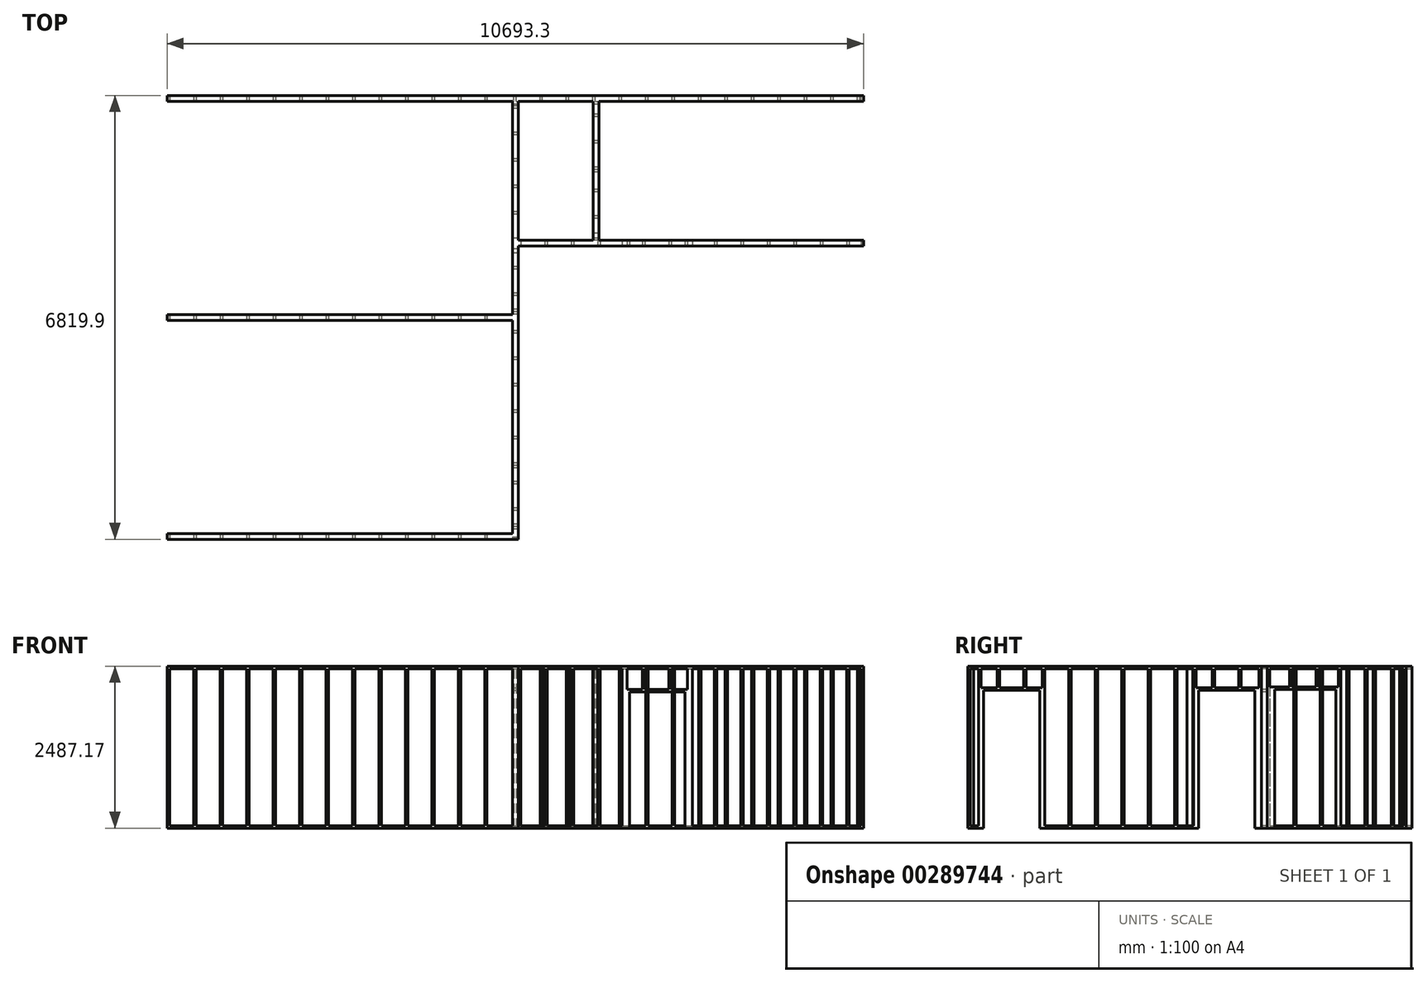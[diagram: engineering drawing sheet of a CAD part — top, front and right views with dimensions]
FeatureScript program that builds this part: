
annotation { "Feature Type Name" : "Feature", "Feature Type Description" : "" }
export const myFeature = defineFeature(function(context is Context, id is Id, definition is map)
    precondition{}
    {
        {
            var Q0;
            Q0=qCreatedBy(makeId("Top.planeOp"),FACE);
            var sketch = newSketch(context, id + "F0", { "sketchPlane" : qUnion([Q0])});
            skLineSegment(sketch, "E0.bottom", {"start": v(5346.65, -4111.3) * mm, "end": v(-5346.65, -4111.3) * mm});
            skLineSegment(sketch, "E0.top", {"start": v(5346.65, 4111.3) * mm, "end": v(-5346.65, 4111.3) * mm});
            skLineSegment(sketch, "E0.left", {"start": v(5346.65, -4111.3) * mm, "end": v(5346.65, 4111.3) * mm});
            skLineSegment(sketch, "E0.right", {"start": v(-5346.65, -4111.3) * mm, "end": v(-5346.65, 4111.3) * mm});
            skPoint(sketch, "E0.middle", {"position": v(0, 0) * mm});
            skLineSegment(sketch, "E1.bottom", {"start": v(-5346.65, 4111.3) * mm, "end": v(5346.65, 4111.3) * mm});
            skLineSegment(sketch, "E1.top", {"start": v(-5346.65, 4022.4) * mm, "end": v(5346.65, 4022.4) * mm});
            skLineSegment(sketch, "E1.left", {"start": v(-5346.65, 4111.3) * mm, "end": v(-5346.65, 4022.4) * mm});
            skLineSegment(sketch, "E1.right", {"start": v(5346.65, 4111.3) * mm, "end": v(5346.65, 4022.4) * mm});
            skLineSegment(sketch, "E2", {"start": v(0, 4111.3) * mm, "end": v(0, -4111.3) * mm, "construction": true});
            skLineSegment(sketch, "E3", {"start": v(-44.45, -2619.7) * mm, "end": v(-5346.65, -2619.7) * mm});
            skLineSegment(sketch, "E4", {"start": v(44.45, 4022.4) * mm, "end": v(44.45, -2708.6) * mm});
            skLineSegment(sketch, "E5", {"start": v(44.45, -2708.6) * mm, "end": v(-5346.65, -2708.6) * mm});
            skLineSegment(sketch, "E6", {"start": v(-44.45, 4022.4) * mm, "end": v(-44.45, -2619.7) * mm});
            skLineSegment(sketch, "E7.bottom", {"start": v(-44.45, 745.8) * mm, "end": v(-5346.65, 745.8) * mm});
            skLineSegment(sketch, "E7.top", {"start": v(-44.45, 656.9) * mm, "end": v(-5346.65, 656.9) * mm});
            skLineSegment(sketch, "E7.left", {"start": v(-44.45, 745.8) * mm, "end": v(-44.45, 656.9) * mm});
            skLineSegment(sketch, "E7.right", {"start": v(-5346.65, 745.8) * mm, "end": v(-5346.65, 656.9) * mm});
            skLineSegment(sketch, "E8.bottom", {"start": v(44.45, 1888.8) * mm, "end": v(5346.65, 1888.8) * mm});
            skLineSegment(sketch, "E8.top", {"start": v(44.45, 1799.9) * mm, "end": v(5346.65, 1799.9) * mm});
            skLineSegment(sketch, "E8.left", {"start": v(44.45, 1888.8) * mm, "end": v(44.45, 1799.9) * mm});
            skLineSegment(sketch, "E8.right", {"start": v(5346.65, 1888.8) * mm, "end": v(5346.65, 1799.9) * mm});
            skLineSegment(sketch, "E9.bottom", {"start": v(1282.55, 1888.8) * mm, "end": v(1193.65, 1888.8) * mm});
            skLineSegment(sketch, "E9.top", {"start": v(1282.55, 4022.4) * mm, "end": v(1193.65, 4022.4) * mm});
            skLineSegment(sketch, "E9.left", {"start": v(1282.55, 1888.8) * mm, "end": v(1282.55, 4022.4) * mm});
            skLineSegment(sketch, "E9.right", {"start": v(1193.65, 1888.8) * mm, "end": v(1193.65, 4022.4) * mm});
            skLineSegment(sketch, "E10", {"start": v(1282.55, 2041.2) * mm, "end": v(1193.65, 2041.2) * mm});
            skLineSegment(sketch, "E11", {"start": v(1282.55, 2955.6) * mm, "end": v(1193.65, 2955.6) * mm});
            skSolve(sketch);
        }
        {
            var Q0;
            {var subQ4=sQuery(id+"F0.wireOp",EDGE,"E0.top");Q0=makeQuery(id+"F0.imprint","IMPRINT",FACE,{"disambiguationData":[TD([[makeQuery(id+"F0.imprint","IMPRINT",EDGE,{"derivedFrom":subQ4}),1.0]])]});}
            var Q1;
            {var subQ7=sQuery(id+"F0.wireOp",EDGE,"E3");Q1=makeQuery(id+"F0.imprint","IMPRINT",FACE,{"disambiguationData":[TD([[makeQuery(id+"F0.imprint","IMPRINT",EDGE,{"derivedFrom":subQ7}),1.0]])]});}
            var Q2;
            {var subQ0=sQuery(id+"F0.wireOp",EDGE,"E8.bottom");Q2=makeQuery(id+"F0.imprint","IMPRINT",FACE,{"disambiguationData":[TD([[makeQuery(id+"F0.imprint","IMPRINT",EDGE,{"derivedFrom":subQ0}),-1.0]])]});}
            var Q3;
            {var subQ0=sQuery(id+"F0.wireOp",EDGE,"E7.bottom");Q3=makeQuery(id+"F0.imprint","IMPRINT",FACE,{"disambiguationData":[TD([[makeQuery(id+"F0.imprint","IMPRINT",EDGE,{"derivedFrom":subQ0}),1.0]])]});}
            var Q4;
            {var subQ5=sQuery(id+"F0.wireOp",EDGE,"E11");Q4=makeQuery(id+"F0.imprint","IMPRINT",FACE,{"disambiguationData":[TD([[makeQuery(id+"F0.imprint","IMPRINT",EDGE,{"derivedFrom":subQ5}),-1.0]])]});}
            var Q5;
            {var subQ5=sQuery(id+"F0.wireOp",EDGE,"E10");Q5=makeQuery(id+"F0.imprint","IMPRINT",FACE,{"disambiguationData":[TD([[makeQuery(id+"F0.imprint","IMPRINT",EDGE,{"derivedFrom":subQ5}),1.0]])]});}
            var Q6;
            {var subQ2=sQuery(id+"F0.wireOp",EDGE,"E10");Q6=makeQuery(id+"F0.imprint","IMPRINT",FACE,{"disambiguationData":[TD([[makeQuery(id+"F0.imprint","IMPRINT",EDGE,{"derivedFrom":subQ2}),-1.0]])]});}
            extrude(context, id + "F1", {"entities" : qUnion([Q0, Q1, Q2, Q3, Q4, Q5, Q6]), "depth" : 2487.17 * mm, "offsetDistance" : 30.48 * mm});
        }
        {
            var Q0;
            {var subQ0=sQuery(id+"F0.wireOp",EDGE,"E4");Q0=makeQuery(id+"F1.opExtrude","SWEPT_FACE",FACE,{"disambiguationData":[OSD([subQ0]),TDD([makeQuery(id+"F0.imprint","IMPRINT",EDGE,{"disambiguationData":[TD([[makeQuery(id+"F0.imprint","INTERSECT",VERTEX,{"derivedFrom":[subQ0,sQuery(id+"F0.wireOp",EDGE,"E8.top")]}),-1.0]])],"derivedFrom":subQ0})])]});}
            var sketch = newSketch(context, id + "F2", { "sketchPlane" : qUnion([Q0])});
            skLineSegment(sketch, "E12.bottom", {"start": v(1698.24, 0) * mm, "end": v(834.75, 0) * mm});
            skLineSegment(sketch, "E12.top", {"start": v(1698.24, 2120.9) * mm, "end": v(834.75, 2120.9) * mm});
            skLineSegment(sketch, "E12.left", {"start": v(1698.24, 0) * mm, "end": v(1698.24, 2120.9) * mm});
            skLineSegment(sketch, "E12.right", {"start": v(834.75, 0) * mm, "end": v(834.75, 2120.9) * mm});
            skLineSegment(sketch, "E13.bottom", {"start": v(-2670.5, 2449.07) * mm, "end": v(758.55, 2449.07) * mm});
            skLineSegment(sketch, "E13.top", {"start": v(-2670.5, 38.1) * mm, "end": v(758.55, 38.1) * mm});
            skLineSegment(sketch, "E13.left", {"start": v(-2670.5, 2449.07) * mm, "end": v(-2670.5, 38.1) * mm});
            skLineSegment(sketch, "E13.right", {"start": v(758.55, 2449.07) * mm, "end": v(758.55, 38.1) * mm});
            skLineSegment(sketch, "E14.bottom", {"start": v(796.65, 2449.07) * mm, "end": v(1761.8, 2449.07) * mm});
            skLineSegment(sketch, "E14.top", {"start": v(796.65, 2159) * mm, "end": v(1761.8, 2159) * mm});
            skLineSegment(sketch, "E14.left", {"start": v(796.65, 2449.07) * mm, "end": v(796.65, 2159) * mm});
            skLineSegment(sketch, "E14.right", {"start": v(1761.8, 2449.07) * mm, "end": v(1761.8, 2159) * mm});
            skLineSegment(sketch, "E15.bottom", {"start": v(-2467.3, 0) * mm, "end": v(-1603.7, 0) * mm});
            skLineSegment(sketch, "E15.top", {"start": v(-2467.3, 2120.9) * mm, "end": v(-1603.7, 2120.9) * mm});
            skLineSegment(sketch, "E15.left", {"start": v(-2467.3, 0) * mm, "end": v(-2467.3, 2120.9) * mm});
            skLineSegment(sketch, "E15.right", {"start": v(-1603.7, 0) * mm, "end": v(-1603.7, 2120.9) * mm});
            skLineSegment(sketch, "E16.bottom", {"start": v(-2467.3, 2120.9) * mm, "end": v(-2505.4, 2120.9) * mm});
            skLineSegment(sketch, "E16.top", {"start": v(-2467.3, 38.1) * mm, "end": v(-2505.4, 38.1) * mm});
            skLineSegment(sketch, "E16.left", {"start": v(-2467.3, 2120.9) * mm, "end": v(-2467.3, 38.1) * mm});
            skLineSegment(sketch, "E16.right", {"start": v(-2505.4, 2120.9) * mm, "end": v(-2505.4, 38.1) * mm});
            skLineSegment(sketch, "E17.bottom", {"start": v(-1603.7, 2120.9) * mm, "end": v(-1565.6, 2120.9) * mm});
            skLineSegment(sketch, "E17.top", {"start": v(-1603.7, 38.1) * mm, "end": v(-1565.6, 38.1) * mm});
            skLineSegment(sketch, "E17.left", {"start": v(-1603.7, 2120.9) * mm, "end": v(-1603.7, 38.1) * mm});
            skLineSegment(sketch, "E17.right", {"start": v(-1565.6, 2120.9) * mm, "end": v(-1565.6, 38.1) * mm});
            skLineSegment(sketch, "E18.bottom", {"start": v(-2505.4, 2120.9) * mm, "end": v(-1565.6, 2120.9) * mm});
            skLineSegment(sketch, "E18.top", {"start": v(-2505.4, 2159) * mm, "end": v(-1565.6, 2159) * mm});
            skLineSegment(sketch, "E18.left", {"start": v(-2505.4, 2120.9) * mm, "end": v(-2505.4, 2159) * mm});
            skLineSegment(sketch, "E18.right", {"start": v(-1565.6, 2120.9) * mm, "end": v(-1565.6, 2159) * mm});
            skLineSegment(sketch, "E19.bottom", {"start": v(-2505.4, 38.1) * mm, "end": v(-2543.5, 38.1) * mm});
            skLineSegment(sketch, "E19.top", {"start": v(-2505.4, 2449.07) * mm, "end": v(-2543.5, 2449.07) * mm});
            skLineSegment(sketch, "E19.left", {"start": v(-2505.4, 38.1) * mm, "end": v(-2505.4, 2449.07) * mm});
            skLineSegment(sketch, "E19.right", {"start": v(-2543.5, 38.1) * mm, "end": v(-2543.5, 2449.07) * mm});
            skLineSegment(sketch, "E20.bottom", {"start": v(-1565.6, 38.1) * mm, "end": v(-1527.5, 38.1) * mm});
            skLineSegment(sketch, "E20.top", {"start": v(-1565.6, 2449.07) * mm, "end": v(-1527.5, 2449.07) * mm});
            skLineSegment(sketch, "E20.left", {"start": v(-1565.6, 38.1) * mm, "end": v(-1565.6, 2449.07) * mm});
            skLineSegment(sketch, "E20.right", {"start": v(-1527.5, 38.1) * mm, "end": v(-1527.5, 2449.07) * mm});
            skLineSegment(sketch, "E21.bottom", {"start": v(-1159.2, 38.1) * mm, "end": v(-1121.1, 38.1) * mm});
            skLineSegment(sketch, "E21.top", {"start": v(-1159.2, 2449.07) * mm, "end": v(-1121.1, 2449.07) * mm});
            skLineSegment(sketch, "E21.left", {"start": v(-1159.2, 38.1) * mm, "end": v(-1159.2, 2449.07) * mm});
            skLineSegment(sketch, "E21.right", {"start": v(-1121.1, 38.1) * mm, "end": v(-1121.1, 2449.07) * mm});
            skLineSegment(sketch, "E22.bottom", {"start": v(-752.9, 38.1) * mm, "end": v(-714.8, 38.1) * mm});
            skLineSegment(sketch, "E22.top", {"start": v(-752.9, 2449.07) * mm, "end": v(-714.8, 2449.07) * mm});
            skLineSegment(sketch, "E22.left", {"start": v(-752.9, 38.1) * mm, "end": v(-752.9, 2449.07) * mm});
            skLineSegment(sketch, "E22.right", {"start": v(-714.8, 38.1) * mm, "end": v(-714.8, 2449.07) * mm});
            skLineSegment(sketch, "E23.bottom", {"start": v(-346.6, 38.1) * mm, "end": v(-308.5, 38.1) * mm});
            skLineSegment(sketch, "E23.top", {"start": v(-346.6, 2449.07) * mm, "end": v(-308.5, 2449.07) * mm});
            skLineSegment(sketch, "E23.left", {"start": v(-346.6, 38.1) * mm, "end": v(-346.6, 2449.07) * mm});
            skLineSegment(sketch, "E23.right", {"start": v(-308.5, 38.1) * mm, "end": v(-308.5, 2449.07) * mm});
            skLineSegment(sketch, "E24.bottom", {"start": v(59.7, 38.1) * mm, "end": v(97.8, 38.1) * mm});
            skLineSegment(sketch, "E24.top", {"start": v(59.7, 2449.07) * mm, "end": v(97.8, 2449.07) * mm});
            skLineSegment(sketch, "E24.left", {"start": v(59.7, 38.1) * mm, "end": v(59.7, 2449.07) * mm});
            skLineSegment(sketch, "E24.right", {"start": v(97.8, 38.1) * mm, "end": v(97.8, 2449.07) * mm});
            skLineSegment(sketch, "E25.bottom", {"start": v(465.99, 2449.07) * mm, "end": v(504.09, 2449.07) * mm});
            skLineSegment(sketch, "E25.top", {"start": v(465.99, 38.1) * mm, "end": v(504.09, 38.1) * mm});
            skLineSegment(sketch, "E25.left", {"start": v(465.99, 2449.07) * mm, "end": v(465.99, 38.1) * mm});
            skLineSegment(sketch, "E25.right", {"start": v(504.09, 2449.07) * mm, "end": v(504.09, 38.1) * mm});
            skLineSegment(sketch, "E26.bottom", {"start": v(-2257.65, 2159) * mm, "end": v(-2219.55, 2159) * mm});
            skLineSegment(sketch, "E26.top", {"start": v(-2257.65, 2449.07) * mm, "end": v(-2219.55, 2449.07) * mm});
            skLineSegment(sketch, "E26.left", {"start": v(-2257.65, 2159) * mm, "end": v(-2257.65, 2449.07) * mm});
            skLineSegment(sketch, "E26.right", {"start": v(-2219.55, 2159) * mm, "end": v(-2219.55, 2449.07) * mm});
            skLineSegment(sketch, "E27.bottom", {"start": v(-1851.36, 2159) * mm, "end": v(-1813.26, 2159) * mm});
            skLineSegment(sketch, "E27.top", {"start": v(-1851.36, 2449.07) * mm, "end": v(-1813.26, 2449.07) * mm});
            skLineSegment(sketch, "E27.left", {"start": v(-1851.36, 2159) * mm, "end": v(-1851.36, 2449.07) * mm});
            skLineSegment(sketch, "E27.right", {"start": v(-1813.26, 2159) * mm, "end": v(-1813.26, 2449.07) * mm});
            skLineSegment(sketch, "E28.bottom", {"start": v(1044.45, 2449.07) * mm, "end": v(1082.55, 2449.07) * mm});
            skLineSegment(sketch, "E28.top", {"start": v(1044.45, 2159) * mm, "end": v(1082.55, 2159) * mm});
            skLineSegment(sketch, "E28.left", {"start": v(1044.45, 2449.07) * mm, "end": v(1044.45, 2159) * mm});
            skLineSegment(sketch, "E28.right", {"start": v(1082.55, 2449.07) * mm, "end": v(1082.55, 2159) * mm});
            skLineSegment(sketch, "E29.bottom", {"start": v(1450.75, 2159) * mm, "end": v(1488.85, 2159) * mm});
            skLineSegment(sketch, "E29.top", {"start": v(1450.75, 2449.07) * mm, "end": v(1488.85, 2449.07) * mm});
            skLineSegment(sketch, "E29.left", {"start": v(1450.75, 2159) * mm, "end": v(1450.75, 2449.07) * mm});
            skLineSegment(sketch, "E29.right", {"start": v(1488.85, 2159) * mm, "end": v(1488.85, 2449.07) * mm});
            skSolve(sketch);
        }
        {
            var Q0;
            Q0=makeQuery(id+"F2.imprint","IMPRINT",FACE,{"disambiguationData":[TD([[makeQuery(id+"F2.imprint","IMPRINT",EDGE,{"derivedFrom":sQuery(id+"F2.wireOp",EDGE,"E12.bottom")}),-1.0]])]});
            var Q1;
            {var subQ5=sQuery(id+"F2.wireOp",EDGE,"E15.top");Q1=makeQuery(id+"F2.imprint","IMPRINT",FACE,{"disambiguationData":[TD([[makeQuery(id+"F2.imprint","IMPRINT",EDGE,{"derivedFrom":subQ5}),-1.0]])]});}
            var Q2;
            {var subQ0=sQuery(id+"F2.wireOp",EDGE,"E19.left");Q2=makeQuery(id+"F2.imprint","IMPRINT",FACE,{"disambiguationData":[TD([[makeQuery(id+"F2.imprint","IMPRINT",EDGE,{"derivedFrom":subQ0}),-1.0]])]});}
            var Q3;
            {var subQ0=sQuery(id+"F2.wireOp",EDGE,"E26.right");Q3=makeQuery(id+"F2.imprint","IMPRINT",FACE,{"disambiguationData":[TD([[makeQuery(id+"F2.imprint","IMPRINT",EDGE,{"derivedFrom":subQ0}),-1.0]])]});}
            var Q4;
            {var subQ0=sQuery(id+"F2.wireOp",EDGE,"E20.left");Q4=makeQuery(id+"F2.imprint","IMPRINT",FACE,{"disambiguationData":[TD([[makeQuery(id+"F2.imprint","IMPRINT",EDGE,{"derivedFrom":subQ0}),1.0]])]});}
            var Q5;
            {var subQ0=sQuery(id+"F2.wireOp",EDGE,"E20.right");Q5=makeQuery(id+"F2.imprint","IMPRINT",FACE,{"disambiguationData":[TD([[makeQuery(id+"F2.imprint","IMPRINT",EDGE,{"derivedFrom":subQ0}),-1.0]])]});}
            var Q6;
            {var subQ0=sQuery(id+"F2.wireOp",EDGE,"E21.right");Q6=makeQuery(id+"F2.imprint","IMPRINT",FACE,{"disambiguationData":[TD([[makeQuery(id+"F2.imprint","IMPRINT",EDGE,{"derivedFrom":subQ0}),-1.0]])]});}
            var Q7;
            {var subQ0=sQuery(id+"F2.wireOp",EDGE,"E22.right");Q7=makeQuery(id+"F2.imprint","IMPRINT",FACE,{"disambiguationData":[TD([[makeQuery(id+"F2.imprint","IMPRINT",EDGE,{"derivedFrom":subQ0}),-1.0]])]});}
            var Q8;
            {var subQ0=sQuery(id+"F2.wireOp",EDGE,"E23.right");Q8=makeQuery(id+"F2.imprint","IMPRINT",FACE,{"disambiguationData":[TD([[makeQuery(id+"F2.imprint","IMPRINT",EDGE,{"derivedFrom":subQ0}),-1.0]])]});}
            var Q9;
            {var subQ0=sQuery(id+"F2.wireOp",EDGE,"E24.right");Q9=makeQuery(id+"F2.imprint","IMPRINT",FACE,{"disambiguationData":[TD([[makeQuery(id+"F2.imprint","IMPRINT",EDGE,{"derivedFrom":subQ0}),-1.0]])]});}
            var Q10;
            {var subQ0=sQuery(id+"F2.wireOp",EDGE,"E13.right");Q10=makeQuery(id+"F2.imprint","IMPRINT",FACE,{"disambiguationData":[TD([[makeQuery(id+"F2.imprint","IMPRINT",EDGE,{"derivedFrom":subQ0}),-1.0]])]});}
            var Q11;
            {var subQ0=sQuery(id+"F2.wireOp",EDGE,"E14.left");Q11=makeQuery(id+"F2.imprint","IMPRINT",FACE,{"disambiguationData":[TD([[makeQuery(id+"F2.imprint","IMPRINT",EDGE,{"derivedFrom":subQ0}),1.0]])]});}
            var Q12;
            {var subQ0=sQuery(id+"F2.wireOp",EDGE,"E28.right");Q12=makeQuery(id+"F2.imprint","IMPRINT",FACE,{"disambiguationData":[TD([[makeQuery(id+"F2.imprint","IMPRINT",EDGE,{"derivedFrom":subQ0}),1.0]])]});}
            var Q13;
            {var subQ2=sQuery(id+"F2.wireOp",EDGE,"E14.right");Q13=makeQuery(id+"F2.imprint","IMPRINT",FACE,{"disambiguationData":[TD([[makeQuery(id+"F2.imprint","IMPRINT",EDGE,{"derivedFrom":subQ2}),-1.0]])]});}
            var Q14;
            {var subQ5=sQuery(id+"F2.wireOp",EDGE,"E15.bottom");Q14=makeQuery(id+"F2.imprint","IMPRINT",FACE,{"disambiguationData":[TD([[makeQuery(id+"F2.imprint","IMPRINT",EDGE,{"derivedFrom":subQ5}),-1.0]])]});}
            var Q15;
            {var subQ0=sQuery(id+"F2.wireOp",EDGE,"E13.left");Q15=makeQuery(id+"F2.imprint","IMPRINT",FACE,{"disambiguationData":[TD([[makeQuery(id+"F2.imprint","IMPRINT",EDGE,{"derivedFrom":subQ0}),1.0]])]});}
            extrude(context, id + "F3", {"entities" : qUnion([Q0, Q1, Q2, Q3, Q4, Q5, Q6, Q7, Q8, Q9, Q10, Q11, Q12, Q13, Q14, Q15]), "operationType" : NewBodyOperationType.REMOVE, "oppositeDirection" : true, "depth" : 88.9 * mm, "offsetDistance" : 30.48 * mm});
        }
        {
            var Q0;
            Q0=makeQuery(id+"F1.opExtrude","SWEPT_FACE",FACE,{"disambiguationData":[OSD([sQuery(id+"F0.wireOp",EDGE,"E5")])]});
            var sketch = newSketch(context, id + "F4", { "sketchPlane" : qUnion([Q0])});
            skLineSegment(sketch, "E30.bottom", {"start": v(-5308.55, 2449.07) * mm, "end": v(-44.45, 2449.07) * mm});
            skLineSegment(sketch, "E30.top", {"start": v(-5308.55, 38.1) * mm, "end": v(-44.45, 38.1) * mm});
            skLineSegment(sketch, "E30.left", {"start": v(-5308.55, 2449.07) * mm, "end": v(-5308.55, 38.1) * mm});
            skLineSegment(sketch, "E30.right", {"start": v(-44.45, 2449.07) * mm, "end": v(-44.45, 38.1) * mm});
            skLineSegment(sketch, "E31.bottom", {"start": v(-4940.35, 2449.07) * mm, "end": v(-4902.25, 2449.07) * mm});
            skLineSegment(sketch, "E31.top", {"start": v(-4940.35, 38.1) * mm, "end": v(-4902.25, 38.1) * mm});
            skLineSegment(sketch, "E31.left", {"start": v(-4940.35, 2449.07) * mm, "end": v(-4940.35, 38.1) * mm});
            skLineSegment(sketch, "E31.right", {"start": v(-4902.25, 2449.07) * mm, "end": v(-4902.25, 38.1) * mm});
            skLineSegment(sketch, "E32.bottom", {"start": v(-4534.05, 2449.07) * mm, "end": v(-4495.95, 2449.07) * mm});
            skLineSegment(sketch, "E32.top", {"start": v(-4534.05, 38.1) * mm, "end": v(-4495.95, 38.1) * mm});
            skLineSegment(sketch, "E32.left", {"start": v(-4534.05, 2449.07) * mm, "end": v(-4534.05, 38.1) * mm});
            skLineSegment(sketch, "E32.right", {"start": v(-4495.95, 2449.07) * mm, "end": v(-4495.95, 38.1) * mm});
            skLineSegment(sketch, "E33.bottom", {"start": v(-4127.75, 2449.07) * mm, "end": v(-4089.65, 2449.07) * mm});
            skLineSegment(sketch, "E33.top", {"start": v(-4127.75, 38.1) * mm, "end": v(-4089.65, 38.1) * mm});
            skLineSegment(sketch, "E33.left", {"start": v(-4127.75, 2449.07) * mm, "end": v(-4127.75, 38.1) * mm});
            skLineSegment(sketch, "E33.right", {"start": v(-4089.65, 2449.07) * mm, "end": v(-4089.65, 38.1) * mm});
            skLineSegment(sketch, "E34.bottom", {"start": v(-3721.46, 2449.07) * mm, "end": v(-3683.36, 2449.07) * mm});
            skLineSegment(sketch, "E34.top", {"start": v(-3721.46, 38.1) * mm, "end": v(-3683.36, 38.1) * mm});
            skLineSegment(sketch, "E34.left", {"start": v(-3721.46, 2449.07) * mm, "end": v(-3721.46, 38.1) * mm});
            skLineSegment(sketch, "E34.right", {"start": v(-3683.36, 2449.07) * mm, "end": v(-3683.36, 38.1) * mm});
            skLineSegment(sketch, "E35.bottom", {"start": v(-3315.16, 2449.07) * mm, "end": v(-3277.06, 2449.07) * mm});
            skLineSegment(sketch, "E35.top", {"start": v(-3315.16, 38.1) * mm, "end": v(-3277.06, 38.1) * mm});
            skLineSegment(sketch, "E35.left", {"start": v(-3315.16, 2449.07) * mm, "end": v(-3315.16, 38.1) * mm});
            skLineSegment(sketch, "E35.right", {"start": v(-3277.06, 2449.07) * mm, "end": v(-3277.06, 38.1) * mm});
            skLineSegment(sketch, "E36.bottom", {"start": v(-2908.86, 2449.07) * mm, "end": v(-2870.76, 2449.07) * mm});
            skLineSegment(sketch, "E36.top", {"start": v(-2908.86, 38.1) * mm, "end": v(-2870.76, 38.1) * mm});
            skLineSegment(sketch, "E36.left", {"start": v(-2908.86, 2449.07) * mm, "end": v(-2908.86, 38.1) * mm});
            skLineSegment(sketch, "E36.right", {"start": v(-2870.76, 2449.07) * mm, "end": v(-2870.76, 38.1) * mm});
            skLineSegment(sketch, "E37.bottom", {"start": v(-2502.56, 2449.07) * mm, "end": v(-2464.46, 2449.07) * mm});
            skLineSegment(sketch, "E37.top", {"start": v(-2502.56, 38.1) * mm, "end": v(-2464.46, 38.1) * mm});
            skLineSegment(sketch, "E37.left", {"start": v(-2502.56, 2449.07) * mm, "end": v(-2502.56, 38.1) * mm});
            skLineSegment(sketch, "E37.right", {"start": v(-2464.46, 2449.07) * mm, "end": v(-2464.46, 38.1) * mm});
            skLineSegment(sketch, "E38.bottom", {"start": v(-2096.26, 2449.07) * mm, "end": v(-2058.16, 2449.07) * mm});
            skLineSegment(sketch, "E38.top", {"start": v(-2096.26, 38.1) * mm, "end": v(-2058.16, 38.1) * mm});
            skLineSegment(sketch, "E38.left", {"start": v(-2096.26, 2449.07) * mm, "end": v(-2096.26, 38.1) * mm});
            skLineSegment(sketch, "E38.right", {"start": v(-2058.16, 2449.07) * mm, "end": v(-2058.16, 38.1) * mm});
            skLineSegment(sketch, "E39.bottom", {"start": v(-1689.96, 2449.07) * mm, "end": v(-1651.86, 2449.07) * mm});
            skLineSegment(sketch, "E39.top", {"start": v(-1689.96, 38.1) * mm, "end": v(-1651.86, 38.1) * mm});
            skLineSegment(sketch, "E39.left", {"start": v(-1689.96, 2449.07) * mm, "end": v(-1689.96, 38.1) * mm});
            skLineSegment(sketch, "E39.right", {"start": v(-1651.86, 2449.07) * mm, "end": v(-1651.86, 38.1) * mm});
            skLineSegment(sketch, "E40.bottom", {"start": v(-1283.67, 2449.07) * mm, "end": v(-1245.57, 2449.07) * mm});
            skLineSegment(sketch, "E40.top", {"start": v(-1283.67, 38.1) * mm, "end": v(-1245.57, 38.1) * mm});
            skLineSegment(sketch, "E40.left", {"start": v(-1283.67, 2449.07) * mm, "end": v(-1283.67, 38.1) * mm});
            skLineSegment(sketch, "E40.right", {"start": v(-1245.57, 2449.07) * mm, "end": v(-1245.57, 38.1) * mm});
            skLineSegment(sketch, "E41.bottom", {"start": v(-877.37, 2449.07) * mm, "end": v(-839.27, 2449.07) * mm});
            skLineSegment(sketch, "E41.top", {"start": v(-877.37, 38.1) * mm, "end": v(-839.27, 38.1) * mm});
            skLineSegment(sketch, "E41.left", {"start": v(-877.37, 2449.07) * mm, "end": v(-877.37, 38.1) * mm});
            skLineSegment(sketch, "E41.right", {"start": v(-839.27, 2449.07) * mm, "end": v(-839.27, 38.1) * mm});
            skLineSegment(sketch, "E42.bottom", {"start": v(-471.07, 2449.07) * mm, "end": v(-432.97, 2449.07) * mm});
            skLineSegment(sketch, "E42.top", {"start": v(-471.07, 38.1) * mm, "end": v(-432.97, 38.1) * mm});
            skLineSegment(sketch, "E42.left", {"start": v(-471.07, 2449.07) * mm, "end": v(-471.07, 38.1) * mm});
            skLineSegment(sketch, "E42.right", {"start": v(-432.97, 2449.07) * mm, "end": v(-432.97, 38.1) * mm});
            skSolve(sketch);
        }
        {
            var Q0;
            {var subQ0=sQuery(id+"F4.wireOp",EDGE,"E30.left");Q0=makeQuery(id+"F4.imprint","IMPRINT",FACE,{"disambiguationData":[TD([[makeQuery(id+"F4.imprint","IMPRINT",EDGE,{"derivedFrom":subQ0}),1.0]])]});}
            var Q1;
            {var subQ0=sQuery(id+"F4.wireOp",EDGE,"E31.right");Q1=makeQuery(id+"F4.imprint","IMPRINT",FACE,{"disambiguationData":[TD([[makeQuery(id+"F4.imprint","IMPRINT",EDGE,{"derivedFrom":subQ0}),1.0]])]});}
            var Q2;
            {var subQ0=sQuery(id+"F4.wireOp",EDGE,"E32.right");Q2=makeQuery(id+"F4.imprint","IMPRINT",FACE,{"disambiguationData":[TD([[makeQuery(id+"F4.imprint","IMPRINT",EDGE,{"derivedFrom":subQ0}),1.0]])]});}
            var Q3;
            {var subQ0=sQuery(id+"F4.wireOp",EDGE,"E33.right");Q3=makeQuery(id+"F4.imprint","IMPRINT",FACE,{"disambiguationData":[TD([[makeQuery(id+"F4.imprint","IMPRINT",EDGE,{"derivedFrom":subQ0}),1.0]])]});}
            var Q4;
            {var subQ0=sQuery(id+"F4.wireOp",EDGE,"E34.right");Q4=makeQuery(id+"F4.imprint","IMPRINT",FACE,{"disambiguationData":[TD([[makeQuery(id+"F4.imprint","IMPRINT",EDGE,{"derivedFrom":subQ0}),1.0]])]});}
            var Q5;
            {var subQ0=sQuery(id+"F4.wireOp",EDGE,"E35.right");Q5=makeQuery(id+"F4.imprint","IMPRINT",FACE,{"disambiguationData":[TD([[makeQuery(id+"F4.imprint","IMPRINT",EDGE,{"derivedFrom":subQ0}),1.0]])]});}
            var Q6;
            {var subQ0=sQuery(id+"F4.wireOp",EDGE,"E36.right");Q6=makeQuery(id+"F4.imprint","IMPRINT",FACE,{"disambiguationData":[TD([[makeQuery(id+"F4.imprint","IMPRINT",EDGE,{"derivedFrom":subQ0}),1.0]])]});}
            var Q7;
            {var subQ0=sQuery(id+"F4.wireOp",EDGE,"E37.right");Q7=makeQuery(id+"F4.imprint","IMPRINT",FACE,{"disambiguationData":[TD([[makeQuery(id+"F4.imprint","IMPRINT",EDGE,{"derivedFrom":subQ0}),1.0]])]});}
            var Q8;
            {var subQ0=sQuery(id+"F4.wireOp",EDGE,"E38.right");Q8=makeQuery(id+"F4.imprint","IMPRINT",FACE,{"disambiguationData":[TD([[makeQuery(id+"F4.imprint","IMPRINT",EDGE,{"derivedFrom":subQ0}),1.0]])]});}
            var Q9;
            {var subQ0=sQuery(id+"F4.wireOp",EDGE,"E39.right");Q9=makeQuery(id+"F4.imprint","IMPRINT",FACE,{"disambiguationData":[TD([[makeQuery(id+"F4.imprint","IMPRINT",EDGE,{"derivedFrom":subQ0}),1.0]])]});}
            var Q10;
            {var subQ0=sQuery(id+"F4.wireOp",EDGE,"E40.right");Q10=makeQuery(id+"F4.imprint","IMPRINT",FACE,{"disambiguationData":[TD([[makeQuery(id+"F4.imprint","IMPRINT",EDGE,{"derivedFrom":subQ0}),1.0]])]});}
            var Q11;
            {var subQ0=sQuery(id+"F4.wireOp",EDGE,"E41.right");Q11=makeQuery(id+"F4.imprint","IMPRINT",FACE,{"disambiguationData":[TD([[makeQuery(id+"F4.imprint","IMPRINT",EDGE,{"derivedFrom":subQ0}),1.0]])]});}
            var Q12;
            {var subQ0=sQuery(id+"F4.wireOp",EDGE,"E30.right");Q12=makeQuery(id+"F4.imprint","IMPRINT",FACE,{"disambiguationData":[TD([[makeQuery(id+"F4.imprint","IMPRINT",EDGE,{"derivedFrom":subQ0}),-1.0]])]});}
            extrude(context, id + "F5", {"entities" : qUnion([Q0, Q1, Q2, Q3, Q4, Q5, Q6, Q7, Q8, Q9, Q10, Q11, Q12]), "operationType" : NewBodyOperationType.REMOVE, "oppositeDirection" : true, "depth" : 7620 * mm, "offsetDistance" : 30.48 * mm});
        }
        {
            var Q0;
            Q0=makeQuery(id+"F1.opExtrude","SWEPT_FACE",FACE,{"disambiguationData":[OSD([sQuery(id+"F0.wireOp",EDGE,"E8.top")])]});
            var sketch = newSketch(context, id + "F6", { "sketchPlane" : qUnion([Q0])});
            skLineSegment(sketch, "E43.bottom", {"start": v(1752.6, 0) * mm, "end": v(2603.5, 0) * mm});
            skLineSegment(sketch, "E43.top", {"start": v(1752.6, 2095.5) * mm, "end": v(2603.5, 2095.5) * mm});
            skLineSegment(sketch, "E43.left", {"start": v(1752.6, 0) * mm, "end": v(1752.6, 2095.5) * mm});
            skLineSegment(sketch, "E43.right", {"start": v(2603.5, 0) * mm, "end": v(2603.5, 2095.5) * mm});
            skLineSegment(sketch, "E44", {"start": v(2178.05, 2095.5) * mm, "end": v(2178.05, 0) * mm, "construction": true});
            skLineSegment(sketch, "E45.bottom", {"start": v(1676.4, 38.1) * mm, "end": v(82.55, 38.1) * mm});
            skLineSegment(sketch, "E45.top", {"start": v(1676.4, 2449.07) * mm, "end": v(82.55, 2449.07) * mm});
            skLineSegment(sketch, "E45.left", {"start": v(1676.4, 38.1) * mm, "end": v(1676.4, 2449.07) * mm});
            skLineSegment(sketch, "E45.right", {"start": v(82.55, 38.1) * mm, "end": v(82.55, 2449.07) * mm});
            skLineSegment(sketch, "E46.bottom", {"start": v(2679.7, 38.1) * mm, "end": v(5308.55, 38.1) * mm});
            skLineSegment(sketch, "E46.top", {"start": v(2679.7, 2449.07) * mm, "end": v(5308.55, 2449.07) * mm});
            skLineSegment(sketch, "E46.left", {"start": v(2679.7, 38.1) * mm, "end": v(2679.7, 2449.07) * mm});
            skLineSegment(sketch, "E46.right", {"start": v(5308.55, 38.1) * mm, "end": v(5308.55, 2449.07) * mm});
            skLineSegment(sketch, "E47.bottom", {"start": v(1714.5, 2449.07) * mm, "end": v(2641.6, 2449.07) * mm});
            skLineSegment(sketch, "E47.top", {"start": v(1714.5, 2133.6) * mm, "end": v(2641.6, 2133.6) * mm});
            skLineSegment(sketch, "E47.left", {"start": v(1714.5, 2449.07) * mm, "end": v(1714.5, 2133.6) * mm});
            skLineSegment(sketch, "E47.right", {"start": v(2641.6, 2449.07) * mm, "end": v(2641.6, 2133.6) * mm});
            skLineSegment(sketch, "E48.bottom", {"start": v(1949.4, 2133.6) * mm, "end": v(1987.5, 2133.6) * mm});
            skLineSegment(sketch, "E48.top", {"start": v(1949.4, 2449.07) * mm, "end": v(1987.5, 2449.07) * mm});
            skLineSegment(sketch, "E48.left", {"start": v(1949.4, 2133.6) * mm, "end": v(1949.4, 2449.07) * mm});
            skLineSegment(sketch, "E48.right", {"start": v(1987.5, 2133.6) * mm, "end": v(1987.5, 2449.07) * mm});
            skLineSegment(sketch, "E49.bottom", {"start": v(2355.7, 2133.6) * mm, "end": v(2393.8, 2133.6) * mm});
            skLineSegment(sketch, "E49.top", {"start": v(2355.7, 2449.07) * mm, "end": v(2393.8, 2449.07) * mm});
            skLineSegment(sketch, "E49.left", {"start": v(2355.7, 2133.6) * mm, "end": v(2355.7, 2449.07) * mm});
            skLineSegment(sketch, "E49.right", {"start": v(2393.8, 2133.6) * mm, "end": v(2393.8, 2449.07) * mm});
            skLineSegment(sketch, "E50.bottom", {"start": v(450.75, 2449.07) * mm, "end": v(488.85, 2449.07) * mm});
            skLineSegment(sketch, "E50.top", {"start": v(450.75, 38.1) * mm, "end": v(488.85, 38.1) * mm});
            skLineSegment(sketch, "E50.left", {"start": v(450.75, 2449.07) * mm, "end": v(450.75, 38.1) * mm});
            skLineSegment(sketch, "E50.right", {"start": v(488.85, 2449.07) * mm, "end": v(488.85, 38.1) * mm});
            skLineSegment(sketch, "E51.bottom", {"start": v(857.05, 2449.07) * mm, "end": v(895.15, 2449.07) * mm});
            skLineSegment(sketch, "E51.top", {"start": v(857.05, 38.1) * mm, "end": v(895.15, 38.1) * mm});
            skLineSegment(sketch, "E51.left", {"start": v(857.05, 2449.07) * mm, "end": v(857.05, 38.1) * mm});
            skLineSegment(sketch, "E51.right", {"start": v(895.15, 2449.07) * mm, "end": v(895.15, 38.1) * mm});
            skLineSegment(sketch, "E52.bottom", {"start": v(1263.35, 2449.07) * mm, "end": v(1301.45, 2449.07) * mm});
            skLineSegment(sketch, "E52.top", {"start": v(1263.35, 38.1) * mm, "end": v(1301.45, 38.1) * mm});
            skLineSegment(sketch, "E52.left", {"start": v(1263.35, 2449.07) * mm, "end": v(1263.35, 38.1) * mm});
            skLineSegment(sketch, "E52.right", {"start": v(1301.45, 2449.07) * mm, "end": v(1301.45, 38.1) * mm});
            skLineSegment(sketch, "E53.bottom", {"start": v(1638.3, 2449.07) * mm, "end": v(1676.4, 2449.07) * mm});
            skLineSegment(sketch, "E53.top", {"start": v(1638.3, 38.1) * mm, "end": v(1676.4, 38.1) * mm});
            skLineSegment(sketch, "E53.left", {"start": v(1638.3, 2449.07) * mm, "end": v(1638.3, 38.1) * mm});
            skLineSegment(sketch, "E53.right", {"start": v(1676.4, 2449.07) * mm, "end": v(1676.4, 38.1) * mm});
            skLineSegment(sketch, "E54.MirrorCS", {"start": v(3905.35, 2449.07) * mm, "end": v(3905.35, 38.1) * mm});
            skLineSegment(sketch, "E55.MirrorCS", {"start": v(3867.25, 2449.07) * mm, "end": v(3867.25, 38.1) * mm});
            skLineSegment(sketch, "E56.MirrorCS", {"start": v(3499.05, 2449.07) * mm, "end": v(3499.05, 38.1) * mm});
            skLineSegment(sketch, "E57.MirrorCS", {"start": v(3460.95, 2449.07) * mm, "end": v(3460.95, 38.1) * mm});
            skLineSegment(sketch, "E58.MirrorCS", {"start": v(3092.75, 2449.07) * mm, "end": v(3092.75, 38.1) * mm});
            skLineSegment(sketch, "E59.MirrorCS", {"start": v(3054.65, 2449.07) * mm, "end": v(3054.65, 38.1) * mm});
            skLineSegment(sketch, "E60.MirrorCS", {"start": v(2717.8, 2449.07) * mm, "end": v(2717.8, 38.1) * mm});
            skLineSegment(sketch, "E61.bottom", {"start": v(4273.55, 2449.07) * mm, "end": v(4311.65, 2449.07) * mm});
            skLineSegment(sketch, "E61.top", {"start": v(4273.55, 38.1) * mm, "end": v(4311.65, 38.1) * mm});
            skLineSegment(sketch, "E61.left", {"start": v(4273.55, 2449.07) * mm, "end": v(4273.55, 38.1) * mm});
            skLineSegment(sketch, "E61.right", {"start": v(4311.65, 2449.07) * mm, "end": v(4311.65, 38.1) * mm});
            skLineSegment(sketch, "E62.bottom", {"start": v(4679.85, 2449.07) * mm, "end": v(4717.95, 2449.07) * mm});
            skLineSegment(sketch, "E62.top", {"start": v(4679.85, 38.1) * mm, "end": v(4717.95, 38.1) * mm});
            skLineSegment(sketch, "E62.left", {"start": v(4679.85, 2449.07) * mm, "end": v(4679.85, 38.1) * mm});
            skLineSegment(sketch, "E62.right", {"start": v(4717.95, 2449.07) * mm, "end": v(4717.95, 38.1) * mm});
            skLineSegment(sketch, "E63.bottom", {"start": v(5086.15, 2449.07) * mm, "end": v(5124.25, 2449.07) * mm});
            skLineSegment(sketch, "E63.top", {"start": v(5086.15, 38.1) * mm, "end": v(5124.25, 38.1) * mm});
            skLineSegment(sketch, "E63.left", {"start": v(5086.15, 2449.07) * mm, "end": v(5086.15, 38.1) * mm});
            skLineSegment(sketch, "E63.right", {"start": v(5124.25, 2449.07) * mm, "end": v(5124.25, 38.1) * mm});
            skLineSegment(sketch, "E64.bottom", {"start": v(5270.45, 2449.07) * mm, "end": v(5308.55, 2449.07) * mm});
            skLineSegment(sketch, "E64.top", {"start": v(5270.45, 38.1) * mm, "end": v(5308.55, 38.1) * mm});
            skLineSegment(sketch, "E64.left", {"start": v(5270.45, 2449.07) * mm, "end": v(5270.45, 38.1) * mm});
            skLineSegment(sketch, "E64.right", {"start": v(5308.55, 2449.07) * mm, "end": v(5308.55, 38.1) * mm});
            skSolve(sketch);
        }
        {
            var Q0;
            {var subQ2=sQuery(id+"F6.wireOp",EDGE,"E45.right");Q0=makeQuery(id+"F6.imprint","IMPRINT",FACE,{"disambiguationData":[TD([[makeQuery(id+"F6.imprint","IMPRINT",EDGE,{"derivedFrom":subQ2}),-1.0]])]});}
            var Q1;
            {var subQ0=sQuery(id+"F6.wireOp",EDGE,"E50.right");Q1=makeQuery(id+"F6.imprint","IMPRINT",FACE,{"disambiguationData":[TD([[makeQuery(id+"F6.imprint","IMPRINT",EDGE,{"derivedFrom":subQ0}),1.0]])]});}
            var Q2;
            {var subQ0=sQuery(id+"F6.wireOp",EDGE,"E51.right");Q2=makeQuery(id+"F6.imprint","IMPRINT",FACE,{"disambiguationData":[TD([[makeQuery(id+"F6.imprint","IMPRINT",EDGE,{"derivedFrom":subQ0}),1.0]])]});}
            var Q3;
            {var subQ0=sQuery(id+"F6.wireOp",EDGE,"E52.right");Q3=makeQuery(id+"F6.imprint","IMPRINT",FACE,{"disambiguationData":[TD([[makeQuery(id+"F6.imprint","IMPRINT",EDGE,{"derivedFrom":subQ0}),1.0]])]});}
            var Q4;
            {var subQ0=sQuery(id+"F6.wireOp",EDGE,"E47.left");Q4=makeQuery(id+"F6.imprint","IMPRINT",FACE,{"disambiguationData":[TD([[makeQuery(id+"F6.imprint","IMPRINT",EDGE,{"derivedFrom":subQ0}),1.0]])]});}
            var Q5;
            Q5=makeQuery(id+"F6.imprint","IMPRINT",FACE,{"disambiguationData":[TD([[makeQuery(id+"F6.imprint","IMPRINT",EDGE,{"derivedFrom":sQuery(id+"F6.wireOp",EDGE,"E43.bottom")}),1.0]])]});
            var Q6;
            {var subQ0=sQuery(id+"F6.wireOp",EDGE,"E47.right");Q6=makeQuery(id+"F6.imprint","IMPRINT",FACE,{"disambiguationData":[TD([[makeQuery(id+"F6.imprint","IMPRINT",EDGE,{"derivedFrom":subQ0}),-1.0]])]});}
            var Q7;
            {var subQ2=sQuery(id+"F6.wireOp",EDGE,"E59.MirrorCS");Q7=makeQuery(id+"F6.imprint","IMPRINT",FACE,{"disambiguationData":[TD([[makeQuery(id+"F6.imprint","IMPRINT",EDGE,{"derivedFrom":subQ2}),-1.0]])]});}
            var Q8;
            {var subQ0=sQuery(id+"F6.wireOp",EDGE,"E57.MirrorCS");Q8=makeQuery(id+"F6.imprint","IMPRINT",FACE,{"disambiguationData":[TD([[makeQuery(id+"F6.imprint","IMPRINT",EDGE,{"derivedFrom":subQ0}),-1.0]])]});}
            var Q9;
            {var subQ0=sQuery(id+"F6.wireOp",EDGE,"E48.right");Q9=makeQuery(id+"F6.imprint","IMPRINT",FACE,{"disambiguationData":[TD([[makeQuery(id+"F6.imprint","IMPRINT",EDGE,{"derivedFrom":subQ0}),-1.0]])]});}
            var Q10;
            {var subQ0=sQuery(id+"F6.wireOp",EDGE,"E55.MirrorCS");Q10=makeQuery(id+"F6.imprint","IMPRINT",FACE,{"disambiguationData":[TD([[makeQuery(id+"F6.imprint","IMPRINT",EDGE,{"derivedFrom":subQ0}),-1.0]])]});}
            var Q11;
            {var subQ2=sQuery(id+"F6.wireOp",EDGE,"E46.right");Q11=makeQuery(id+"F6.imprint","IMPRINT",FACE,{"disambiguationData":[TD([[makeQuery(id+"F6.imprint","IMPRINT",EDGE,{"derivedFrom":subQ2}),1.0]])]});}
            var Q12;
            {var subQ0=sQuery(id+"F6.wireOp",EDGE,"E54.MirrorCS");Q12=makeQuery(id+"F6.imprint","IMPRINT",FACE,{"disambiguationData":[TD([[makeQuery(id+"F6.imprint","IMPRINT",EDGE,{"derivedFrom":subQ0}),1.0]])]});}
            var Q13;
            {var subQ0=sQuery(id+"F6.wireOp",EDGE,"E61.right");Q13=makeQuery(id+"F6.imprint","IMPRINT",FACE,{"disambiguationData":[TD([[makeQuery(id+"F6.imprint","IMPRINT",EDGE,{"derivedFrom":subQ0}),1.0]])]});}
            var Q14;
            {var subQ0=sQuery(id+"F6.wireOp",EDGE,"E62.right");Q14=makeQuery(id+"F6.imprint","IMPRINT",FACE,{"disambiguationData":[TD([[makeQuery(id+"F6.imprint","IMPRINT",EDGE,{"derivedFrom":subQ0}),1.0]])]});}
            var Q15;
            {var subQ0=sQuery(id+"F6.wireOp",EDGE,"E63.right");Q15=makeQuery(id+"F6.imprint","IMPRINT",FACE,{"disambiguationData":[TD([[makeQuery(id+"F6.imprint","IMPRINT",EDGE,{"derivedFrom":subQ0}),1.0]])]});}
            extrude(context, id + "F7", {"entities" : qUnion([Q0, Q1, Q2, Q3, Q4, Q5, Q6, Q7, Q8, Q9, Q10, Q11, Q12, Q13, Q14, Q15]), "operationType" : NewBodyOperationType.REMOVE, "oppositeDirection" : true, "depth" : 88.9 * mm, "offsetDistance" : 30.48 * mm});
        }
        {
            var Q0;
            Q0=makeQuery(id+"F1.opExtrude","SWEPT_FACE",FACE,{"disambiguationData":[OSD([sQuery(id+"F0.wireOp",EDGE,"E0.top")])]});
            var sketch = newSketch(context, id + "F8", { "sketchPlane" : qUnion([Q0])});
            skLineSegment(sketch, "E65.bottom", {"start": v(44.45, 2449.07) * mm, "end": v(26.67, 2449.07) * mm});
            skLineSegment(sketch, "E65.top", {"start": v(44.45, 38.1) * mm, "end": v(26.67, 38.1) * mm});
            skLineSegment(sketch, "E65.left", {"start": v(44.45, 2449.07) * mm, "end": v(44.45, 38.1) * mm});
            skLineSegment(sketch, "E65.right", {"start": v(26.67, 2449.07) * mm, "end": v(26.67, 38.1) * mm});
            skLineSegment(sketch, "E66.bottom", {"start": v(-11.43, 2449.07) * mm, "end": v(-5308.55, 2449.07) * mm});
            skLineSegment(sketch, "E66.top", {"start": v(-11.43, 38.1) * mm, "end": v(-5308.55, 38.1) * mm});
            skLineSegment(sketch, "E66.left", {"start": v(-11.43, 2449.07) * mm, "end": v(-11.43, 38.1) * mm});
            skLineSegment(sketch, "E66.right", {"start": v(-5308.55, 2449.07) * mm, "end": v(-5308.55, 38.1) * mm});
            skLineSegment(sketch, "E67.bottom", {"start": v(-379.63, 2449.07) * mm, "end": v(-417.73, 2449.07) * mm});
            skLineSegment(sketch, "E67.top", {"start": v(-379.63, 38.1) * mm, "end": v(-417.73, 38.1) * mm});
            skLineSegment(sketch, "E67.left", {"start": v(-379.63, 2449.07) * mm, "end": v(-379.63, 38.1) * mm});
            skLineSegment(sketch, "E67.right", {"start": v(-417.73, 2449.07) * mm, "end": v(-417.73, 38.1) * mm});
            skLineSegment(sketch, "E68.bottom", {"start": v(-785.93, 2449.07) * mm, "end": v(-824.03, 2449.07) * mm});
            skLineSegment(sketch, "E68.top", {"start": v(-785.93, 38.1) * mm, "end": v(-824.03, 38.1) * mm});
            skLineSegment(sketch, "E68.left", {"start": v(-785.93, 2449.07) * mm, "end": v(-785.93, 38.1) * mm});
            skLineSegment(sketch, "E68.right", {"start": v(-824.03, 2449.07) * mm, "end": v(-824.03, 38.1) * mm});
            skLineSegment(sketch, "E69.bottom", {"start": v(-1192.23, 2449.07) * mm, "end": v(-1230.33, 2449.07) * mm});
            skLineSegment(sketch, "E69.top", {"start": v(-1192.23, 38.1) * mm, "end": v(-1230.33, 38.1) * mm});
            skLineSegment(sketch, "E69.left", {"start": v(-1192.23, 2449.07) * mm, "end": v(-1192.23, 38.1) * mm});
            skLineSegment(sketch, "E69.right", {"start": v(-1230.33, 2449.07) * mm, "end": v(-1230.33, 38.1) * mm});
            skLineSegment(sketch, "E70.bottom", {"start": v(-1598.52, 2449.07) * mm, "end": v(-1636.62, 2449.07) * mm});
            skLineSegment(sketch, "E70.top", {"start": v(-1598.52, 38.1) * mm, "end": v(-1636.62, 38.1) * mm});
            skLineSegment(sketch, "E70.left", {"start": v(-1598.52, 2449.07) * mm, "end": v(-1598.52, 38.1) * mm});
            skLineSegment(sketch, "E70.right", {"start": v(-1636.62, 2449.07) * mm, "end": v(-1636.62, 38.1) * mm});
            skLineSegment(sketch, "E71.bottom", {"start": v(-2004.82, 2449.07) * mm, "end": v(-2042.92, 2449.07) * mm});
            skLineSegment(sketch, "E71.top", {"start": v(-2004.82, 38.1) * mm, "end": v(-2042.92, 38.1) * mm});
            skLineSegment(sketch, "E71.left", {"start": v(-2004.82, 2449.07) * mm, "end": v(-2004.82, 38.1) * mm});
            skLineSegment(sketch, "E71.right", {"start": v(-2042.92, 2449.07) * mm, "end": v(-2042.92, 38.1) * mm});
            skLineSegment(sketch, "E72.bottom", {"start": v(-2411.12, 2449.07) * mm, "end": v(-2449.22, 2449.07) * mm});
            skLineSegment(sketch, "E72.top", {"start": v(-2411.12, 38.1) * mm, "end": v(-2449.22, 38.1) * mm});
            skLineSegment(sketch, "E72.left", {"start": v(-2411.12, 2449.07) * mm, "end": v(-2411.12, 38.1) * mm});
            skLineSegment(sketch, "E72.right", {"start": v(-2449.22, 2449.07) * mm, "end": v(-2449.22, 38.1) * mm});
            skLineSegment(sketch, "E73.bottom", {"start": v(-2817.42, 2449.07) * mm, "end": v(-2855.52, 2449.07) * mm});
            skLineSegment(sketch, "E73.top", {"start": v(-2817.42, 38.1) * mm, "end": v(-2855.52, 38.1) * mm});
            skLineSegment(sketch, "E73.left", {"start": v(-2817.42, 2449.07) * mm, "end": v(-2817.42, 38.1) * mm});
            skLineSegment(sketch, "E73.right", {"start": v(-2855.52, 2449.07) * mm, "end": v(-2855.52, 38.1) * mm});
            skLineSegment(sketch, "E74.bottom", {"start": v(-3223.72, 2449.07) * mm, "end": v(-3261.82, 2449.07) * mm});
            skLineSegment(sketch, "E74.top", {"start": v(-3223.72, 38.1) * mm, "end": v(-3261.82, 38.1) * mm});
            skLineSegment(sketch, "E74.left", {"start": v(-3223.72, 2449.07) * mm, "end": v(-3223.72, 38.1) * mm});
            skLineSegment(sketch, "E74.right", {"start": v(-3261.82, 2449.07) * mm, "end": v(-3261.82, 38.1) * mm});
            skLineSegment(sketch, "E75.bottom", {"start": v(-3630.02, 2449.07) * mm, "end": v(-3668.12, 2449.07) * mm});
            skLineSegment(sketch, "E75.top", {"start": v(-3630.02, 38.1) * mm, "end": v(-3668.12, 38.1) * mm});
            skLineSegment(sketch, "E75.left", {"start": v(-3630.02, 2449.07) * mm, "end": v(-3630.02, 38.1) * mm});
            skLineSegment(sketch, "E75.right", {"start": v(-3668.12, 2449.07) * mm, "end": v(-3668.12, 38.1) * mm});
            skLineSegment(sketch, "E76.bottom", {"start": v(-4036.31, 2449.07) * mm, "end": v(-4074.41, 2449.07) * mm});
            skLineSegment(sketch, "E76.top", {"start": v(-4036.31, 38.1) * mm, "end": v(-4074.41, 38.1) * mm});
            skLineSegment(sketch, "E76.left", {"start": v(-4036.31, 2449.07) * mm, "end": v(-4036.31, 38.1) * mm});
            skLineSegment(sketch, "E76.right", {"start": v(-4074.41, 2449.07) * mm, "end": v(-4074.41, 38.1) * mm});
            skLineSegment(sketch, "E77.bottom", {"start": v(-4442.61, 2449.07) * mm, "end": v(-4480.71, 2449.07) * mm});
            skLineSegment(sketch, "E77.top", {"start": v(-4442.61, 38.1) * mm, "end": v(-4480.71, 38.1) * mm});
            skLineSegment(sketch, "E77.left", {"start": v(-4442.61, 2449.07) * mm, "end": v(-4442.61, 38.1) * mm});
            skLineSegment(sketch, "E77.right", {"start": v(-4480.71, 2449.07) * mm, "end": v(-4480.71, 38.1) * mm});
            skLineSegment(sketch, "E78.bottom", {"start": v(-4848.91, 2449.07) * mm, "end": v(-4887.01, 2449.07) * mm});
            skLineSegment(sketch, "E78.top", {"start": v(-4848.91, 38.1) * mm, "end": v(-4887.01, 38.1) * mm});
            skLineSegment(sketch, "E78.left", {"start": v(-4848.91, 2449.07) * mm, "end": v(-4848.91, 38.1) * mm});
            skLineSegment(sketch, "E78.right", {"start": v(-4887.01, 2449.07) * mm, "end": v(-4887.01, 38.1) * mm});
            skLineSegment(sketch, "E79.bottom", {"start": v(-5255.2, 2449.07) * mm, "end": v(-5293.3, 2449.07) * mm});
            skLineSegment(sketch, "E79.top", {"start": v(-5255.2, 38.1) * mm, "end": v(-5293.3, 38.1) * mm});
            skLineSegment(sketch, "E79.left", {"start": v(-5255.2, 2449.07) * mm, "end": v(-5255.2, 38.1) * mm});
            skLineSegment(sketch, "E79.right", {"start": v(-5293.3, 2449.07) * mm, "end": v(-5293.3, 38.1) * mm});
            skSolve(sketch);
        }
        {
            var Q0;
            {var subQ2=sQuery(id+"F8.wireOp",EDGE,"E66.right");Q0=makeQuery(id+"F8.imprint","IMPRINT",FACE,{"disambiguationData":[TD([[makeQuery(id+"F8.imprint","IMPRINT",EDGE,{"derivedFrom":subQ2}),1.0]])]});}
            var Q1;
            {var subQ0=sQuery(id+"F8.wireOp",EDGE,"E76.right");Q1=makeQuery(id+"F8.imprint","IMPRINT",FACE,{"disambiguationData":[TD([[makeQuery(id+"F8.imprint","IMPRINT",EDGE,{"derivedFrom":subQ0}),-1.0]])]});}
            var Q2;
            {var subQ0=sQuery(id+"F8.wireOp",EDGE,"E75.right");Q2=makeQuery(id+"F8.imprint","IMPRINT",FACE,{"disambiguationData":[TD([[makeQuery(id+"F8.imprint","IMPRINT",EDGE,{"derivedFrom":subQ0}),-1.0]])]});}
            var Q3;
            {var subQ0=sQuery(id+"F8.wireOp",EDGE,"E74.right");Q3=makeQuery(id+"F8.imprint","IMPRINT",FACE,{"disambiguationData":[TD([[makeQuery(id+"F8.imprint","IMPRINT",EDGE,{"derivedFrom":subQ0}),-1.0]])]});}
            var Q4;
            {var subQ0=sQuery(id+"F8.wireOp",EDGE,"E73.right");Q4=makeQuery(id+"F8.imprint","IMPRINT",FACE,{"disambiguationData":[TD([[makeQuery(id+"F8.imprint","IMPRINT",EDGE,{"derivedFrom":subQ0}),-1.0]])]});}
            var Q5;
            {var subQ0=sQuery(id+"F8.wireOp",EDGE,"E72.right");Q5=makeQuery(id+"F8.imprint","IMPRINT",FACE,{"disambiguationData":[TD([[makeQuery(id+"F8.imprint","IMPRINT",EDGE,{"derivedFrom":subQ0}),-1.0]])]});}
            var Q6;
            {var subQ0=sQuery(id+"F8.wireOp",EDGE,"E71.right");Q6=makeQuery(id+"F8.imprint","IMPRINT",FACE,{"disambiguationData":[TD([[makeQuery(id+"F8.imprint","IMPRINT",EDGE,{"derivedFrom":subQ0}),-1.0]])]});}
            var Q7;
            {var subQ0=sQuery(id+"F8.wireOp",EDGE,"E70.right");Q7=makeQuery(id+"F8.imprint","IMPRINT",FACE,{"disambiguationData":[TD([[makeQuery(id+"F8.imprint","IMPRINT",EDGE,{"derivedFrom":subQ0}),-1.0]])]});}
            var Q8;
            {var subQ0=sQuery(id+"F8.wireOp",EDGE,"E69.right");Q8=makeQuery(id+"F8.imprint","IMPRINT",FACE,{"disambiguationData":[TD([[makeQuery(id+"F8.imprint","IMPRINT",EDGE,{"derivedFrom":subQ0}),-1.0]])]});}
            var Q9;
            {var subQ0=sQuery(id+"F8.wireOp",EDGE,"E68.right");Q9=makeQuery(id+"F8.imprint","IMPRINT",FACE,{"disambiguationData":[TD([[makeQuery(id+"F8.imprint","IMPRINT",EDGE,{"derivedFrom":subQ0}),-1.0]])]});}
            var Q10;
            {var subQ0=sQuery(id+"F8.wireOp",EDGE,"E67.right");Q10=makeQuery(id+"F8.imprint","IMPRINT",FACE,{"disambiguationData":[TD([[makeQuery(id+"F8.imprint","IMPRINT",EDGE,{"derivedFrom":subQ0}),-1.0]])]});}
            var Q11;
            {var subQ0=sQuery(id+"F8.wireOp",EDGE,"E66.left");Q11=makeQuery(id+"F8.imprint","IMPRINT",FACE,{"disambiguationData":[TD([[makeQuery(id+"F8.imprint","IMPRINT",EDGE,{"derivedFrom":subQ0}),-1.0]])]});}
            var Q12;
            Q12=makeQuery(id+"F8.imprint","IMPRINT",FACE,{"disambiguationData":[TD([[makeQuery(id+"F8.imprint","IMPRINT",EDGE,{"derivedFrom":sQuery(id+"F8.wireOp",EDGE,"E65.bottom")}),1.0]])]});
            var Q13;
            {var subQ0=sQuery(id+"F8.wireOp",EDGE,"E77.right");Q13=makeQuery(id+"F8.imprint","IMPRINT",FACE,{"disambiguationData":[TD([[makeQuery(id+"F8.imprint","IMPRINT",EDGE,{"derivedFrom":subQ0}),-1.0]])]});}
            var Q14;
            {var subQ0=sQuery(id+"F8.wireOp",EDGE,"E78.right");Q14=makeQuery(id+"F8.imprint","IMPRINT",FACE,{"disambiguationData":[TD([[makeQuery(id+"F8.imprint","IMPRINT",EDGE,{"derivedFrom":subQ0}),-1.0]])]});}
            extrude(context, id + "F9", {"entities" : qUnion([Q0, Q1, Q2, Q3, Q4, Q5, Q6, Q7, Q8, Q9, Q10, Q11, Q12, Q13, Q14]), "operationType" : NewBodyOperationType.REMOVE, "oppositeDirection" : true, "depth" : 88.9 * mm, "offsetDistance" : 30.48 * mm});
        }
        {
            var Q0;
            {var subQ0=sQuery(id+"F0.wireOp",EDGE,"E4");Q0=makeQuery(id+"F1.opExtrude","SWEPT_FACE",FACE,{"disambiguationData":[OSD([subQ0]),TDD([makeQuery(id+"F0.imprint","IMPRINT",EDGE,{"disambiguationData":[TD([[makeQuery(id+"F0.imprint","INTERSECT",VERTEX,{"derivedFrom":[sQuery(id+"F0.wireOp",EDGE,"E1.top"),subQ0]}),-1.0]])],"derivedFrom":subQ0})])]});}
            var sketch = newSketch(context, id + "F10", { "sketchPlane" : qUnion([Q0])});
            skLineSegment(sketch, "E80.bottom", {"start": v(1926.9, 2449.07) * mm, "end": v(3984.3, 2449.07) * mm});
            skLineSegment(sketch, "E80.top", {"start": v(1926.9, 38.1) * mm, "end": v(3984.3, 38.1) * mm});
            skLineSegment(sketch, "E80.left", {"start": v(1926.9, 2449.07) * mm, "end": v(1926.9, 38.1) * mm});
            skLineSegment(sketch, "E80.right", {"start": v(3984.3, 2449.07) * mm, "end": v(3984.3, 38.1) * mm});
            skLineSegment(sketch, "E81.bottom", {"start": v(2295.1, 2449.07) * mm, "end": v(2333.2, 2449.07) * mm});
            skLineSegment(sketch, "E81.top", {"start": v(2295.1, 38.1) * mm, "end": v(2333.2, 38.1) * mm});
            skLineSegment(sketch, "E81.left", {"start": v(2295.1, 2449.07) * mm, "end": v(2295.1, 38.1) * mm});
            skLineSegment(sketch, "E81.right", {"start": v(2333.2, 2449.07) * mm, "end": v(2333.2, 38.1) * mm});
            skLineSegment(sketch, "E82.bottom", {"start": v(2701.4, 2449.07) * mm, "end": v(2739.5, 2449.07) * mm});
            skLineSegment(sketch, "E82.top", {"start": v(2701.4, 38.1) * mm, "end": v(2739.5, 38.1) * mm});
            skLineSegment(sketch, "E82.left", {"start": v(2701.4, 2449.07) * mm, "end": v(2701.4, 38.1) * mm});
            skLineSegment(sketch, "E82.right", {"start": v(2739.5, 2449.07) * mm, "end": v(2739.5, 38.1) * mm});
            skLineSegment(sketch, "E83.bottom", {"start": v(3107.7, 2449.07) * mm, "end": v(3145.8, 2449.07) * mm});
            skLineSegment(sketch, "E83.top", {"start": v(3107.7, 38.1) * mm, "end": v(3145.8, 38.1) * mm});
            skLineSegment(sketch, "E83.left", {"start": v(3107.7, 2449.07) * mm, "end": v(3107.7, 38.1) * mm});
            skLineSegment(sketch, "E83.right", {"start": v(3145.8, 2449.07) * mm, "end": v(3145.8, 38.1) * mm});
            skLineSegment(sketch, "E84.bottom", {"start": v(3513.99, 2449.07) * mm, "end": v(3552.09, 2449.07) * mm});
            skLineSegment(sketch, "E84.top", {"start": v(3513.99, 38.1) * mm, "end": v(3552.09, 38.1) * mm});
            skLineSegment(sketch, "E84.left", {"start": v(3513.99, 2449.07) * mm, "end": v(3513.99, 38.1) * mm});
            skLineSegment(sketch, "E84.right", {"start": v(3552.09, 2449.07) * mm, "end": v(3552.09, 38.1) * mm});
            skLineSegment(sketch, "E85.bottom", {"start": v(3920.29, 2449.07) * mm, "end": v(3958.39, 2449.07) * mm});
            skLineSegment(sketch, "E85.top", {"start": v(3920.29, 38.1) * mm, "end": v(3958.39, 38.1) * mm});
            skLineSegment(sketch, "E85.left", {"start": v(3920.29, 2449.07) * mm, "end": v(3920.29, 38.1) * mm});
            skLineSegment(sketch, "E85.right", {"start": v(3958.39, 2449.07) * mm, "end": v(3958.39, 38.1) * mm});
            skSolve(sketch);
        }
        {
            var Q0;
            {var subQ0=sQuery(id+"F10.wireOp",EDGE,"E80.left");Q0=makeQuery(id+"F10.imprint","IMPRINT",FACE,{"disambiguationData":[TD([[makeQuery(id+"F10.imprint","IMPRINT",EDGE,{"derivedFrom":subQ0}),1.0]])]});}
            var Q1;
            {var subQ0=sQuery(id+"F10.wireOp",EDGE,"E81.right");Q1=makeQuery(id+"F10.imprint","IMPRINT",FACE,{"disambiguationData":[TD([[makeQuery(id+"F10.imprint","IMPRINT",EDGE,{"derivedFrom":subQ0}),1.0]])]});}
            var Q2;
            {var subQ0=sQuery(id+"F10.wireOp",EDGE,"E82.right");Q2=makeQuery(id+"F10.imprint","IMPRINT",FACE,{"disambiguationData":[TD([[makeQuery(id+"F10.imprint","IMPRINT",EDGE,{"derivedFrom":subQ0}),1.0]])]});}
            var Q3;
            {var subQ0=sQuery(id+"F10.wireOp",EDGE,"E83.right");Q3=makeQuery(id+"F10.imprint","IMPRINT",FACE,{"disambiguationData":[TD([[makeQuery(id+"F10.imprint","IMPRINT",EDGE,{"derivedFrom":subQ0}),1.0]])]});}
            var Q4;
            {var subQ0=sQuery(id+"F10.wireOp",EDGE,"E84.right");Q4=makeQuery(id+"F10.imprint","IMPRINT",FACE,{"disambiguationData":[TD([[makeQuery(id+"F10.imprint","IMPRINT",EDGE,{"derivedFrom":subQ0}),1.0]])]});}
            var Q5;
            {var subQ0=sQuery(id+"F10.wireOp",EDGE,"E80.right");Q5=makeQuery(id+"F10.imprint","IMPRINT",FACE,{"disambiguationData":[TD([[makeQuery(id+"F10.imprint","IMPRINT",EDGE,{"derivedFrom":subQ0}),-1.0]])]});}
            extrude(context, id + "F11", {"entities" : qUnion([Q0, Q1, Q2, Q3, Q4, Q5]), "operationType" : NewBodyOperationType.REMOVE, "oppositeDirection" : true, "depth" : 88.9 * mm, "offsetDistance" : 30.48 * mm});
        }
        {
            var Q0;
            Q0=makeQuery(id+"F1.opExtrude","SWEPT_FACE",FACE,{"disambiguationData":[OSD([sQuery(id+"F0.wireOp",EDGE,"E9.left")])]});
            var sketch = newSketch(context, id + "F12", { "sketchPlane" : qUnion([Q0])});
            skSolve(sketch);
        }
        {
            var Q0;
            {var subQ7=sQuery(id+"F0.wireOp",EDGE,"E9.left");Q0=makeQuery(id+"F12.imprint","IMPRINT",FACE,{"disambiguationData":[TD([[makeQuery(id+"F12.imprint","IMPRINT",EDGE,{"derivedFrom":makeQuery(id+"F1.opExtrude","CAP_EDGE",EDGE,{"disambiguationData":[OSD([subQ7])],"isStart":true})}),1.0]])]});}
            var sketch = newSketch(context, id + "F13", { "sketchPlane" : qUnion([Q0])});
            skLineSegment(sketch, "E86.bottom", {"start": v(2003.1, 2133.6) * mm, "end": v(2942.9, 2133.6) * mm});
            skLineSegment(sketch, "E86.top", {"start": v(2003.1, 0) * mm, "end": v(2942.9, 0) * mm});
            skLineSegment(sketch, "E86.left", {"start": v(2003.1, 2133.6) * mm, "end": v(2003.1, 0) * mm});
            skLineSegment(sketch, "E86.right", {"start": v(2942.9, 2133.6) * mm, "end": v(2942.9, 0) * mm});
            skLineSegment(sketch, "E87.bottom", {"start": v(1926.9, 2171.7) * mm, "end": v(2981, 2171.7) * mm});
            skLineSegment(sketch, "E87.top", {"start": v(1926.9, 2449.07) * mm, "end": v(2981, 2449.07) * mm});
            skLineSegment(sketch, "E87.left", {"start": v(1926.9, 2171.7) * mm, "end": v(1926.9, 2449.07) * mm});
            skLineSegment(sketch, "E87.right", {"start": v(2981, 2171.7) * mm, "end": v(2981, 2449.07) * mm});
            skLineSegment(sketch, "E88.bottom", {"start": v(2231.8, 2171.7) * mm, "end": v(2269.9, 2171.7) * mm});
            skLineSegment(sketch, "E88.top", {"start": v(2231.8, 2449.07) * mm, "end": v(2269.9, 2449.07) * mm});
            skLineSegment(sketch, "E88.left", {"start": v(2231.8, 2171.7) * mm, "end": v(2231.8, 2449.07) * mm});
            skLineSegment(sketch, "E88.right", {"start": v(2269.9, 2171.7) * mm, "end": v(2269.9, 2449.07) * mm});
            skLineSegment(sketch, "E89.bottom", {"start": v(2638.1, 2171.7) * mm, "end": v(2676.2, 2171.7) * mm});
            skLineSegment(sketch, "E89.top", {"start": v(2638.1, 2449.07) * mm, "end": v(2676.2, 2449.07) * mm});
            skLineSegment(sketch, "E89.left", {"start": v(2638.1, 2171.7) * mm, "end": v(2638.1, 2449.07) * mm});
            skLineSegment(sketch, "E89.right", {"start": v(2676.2, 2171.7) * mm, "end": v(2676.2, 2449.07) * mm});
            skLineSegment(sketch, "E90.bottom", {"start": v(3019.1, 2449.07) * mm, "end": v(3984.3, 2449.07) * mm});
            skLineSegment(sketch, "E90.top", {"start": v(3019.1, 38.1) * mm, "end": v(3984.3, 38.1) * mm});
            skLineSegment(sketch, "E90.left", {"start": v(3019.1, 2449.07) * mm, "end": v(3019.1, 38.1) * mm});
            skLineSegment(sketch, "E90.right", {"start": v(3984.3, 2449.07) * mm, "end": v(3984.3, 38.1) * mm});
            skLineSegment(sketch, "E91.bottom", {"start": v(3387.3, 2449.07) * mm, "end": v(3425.4, 2449.07) * mm});
            skLineSegment(sketch, "E91.top", {"start": v(3387.3, 38.1) * mm, "end": v(3425.4, 38.1) * mm});
            skLineSegment(sketch, "E91.left", {"start": v(3387.3, 2449.07) * mm, "end": v(3387.3, 38.1) * mm});
            skLineSegment(sketch, "E91.right", {"start": v(3425.4, 2449.07) * mm, "end": v(3425.4, 38.1) * mm});
            skLineSegment(sketch, "E92.bottom", {"start": v(3793.6, 2449.07) * mm, "end": v(3831.7, 2449.07) * mm});
            skLineSegment(sketch, "E92.top", {"start": v(3793.6, 38.1) * mm, "end": v(3831.7, 38.1) * mm});
            skLineSegment(sketch, "E92.left", {"start": v(3793.6, 2449.07) * mm, "end": v(3793.6, 38.1) * mm});
            skLineSegment(sketch, "E92.right", {"start": v(3831.7, 2449.07) * mm, "end": v(3831.7, 38.1) * mm});
            skSolve(sketch);
        }
        {
            var Q0;
            {var subQ0=sQuery(id+"F13.wireOp",EDGE,"E90.left");Q0=makeQuery(id+"F13.imprint","IMPRINT",FACE,{"disambiguationData":[TD([[makeQuery(id+"F13.imprint","IMPRINT",EDGE,{"derivedFrom":subQ0}),1.0]])]});}
            var Q1;
            {var subQ0=sQuery(id+"F13.wireOp",EDGE,"E91.right");Q1=makeQuery(id+"F13.imprint","IMPRINT",FACE,{"disambiguationData":[TD([[makeQuery(id+"F13.imprint","IMPRINT",EDGE,{"derivedFrom":subQ0}),1.0]])]});}
            var Q2;
            {var subQ0=sQuery(id+"F13.wireOp",EDGE,"E90.right");Q2=makeQuery(id+"F13.imprint","IMPRINT",FACE,{"disambiguationData":[TD([[makeQuery(id+"F13.imprint","IMPRINT",EDGE,{"derivedFrom":subQ0}),-1.0]])]});}
            var Q3;
            {var subQ0=sQuery(id+"F13.wireOp",EDGE,"E87.right");Q3=makeQuery(id+"F13.imprint","IMPRINT",FACE,{"disambiguationData":[TD([[makeQuery(id+"F13.imprint","IMPRINT",EDGE,{"derivedFrom":subQ0}),1.0]])]});}
            var Q4;
            {var subQ0=sQuery(id+"F13.wireOp",EDGE,"E88.right");Q4=makeQuery(id+"F13.imprint","IMPRINT",FACE,{"disambiguationData":[TD([[makeQuery(id+"F13.imprint","IMPRINT",EDGE,{"derivedFrom":subQ0}),-1.0]])]});}
            var Q5;
            {var subQ0=sQuery(id+"F13.wireOp",EDGE,"E87.left");Q5=makeQuery(id+"F13.imprint","IMPRINT",FACE,{"disambiguationData":[TD([[makeQuery(id+"F13.imprint","IMPRINT",EDGE,{"derivedFrom":subQ0}),-1.0]])]});}
            var Q6;
            Q6=makeQuery(id+"F13.imprint","IMPRINT",FACE,{"disambiguationData":[TD([[makeQuery(id+"F13.imprint","IMPRINT",EDGE,{"derivedFrom":sQuery(id+"F13.wireOp",EDGE,"E86.bottom")}),-1.0]])]});
            extrude(context, id + "F14", {"entities" : qUnion([Q0, Q1, Q2, Q3, Q4, Q5, Q6]), "operationType" : NewBodyOperationType.REMOVE, "oppositeDirection" : true, "depth" : 88.9 * mm, "offsetDistance" : 30.48 * mm});
        }
    });
